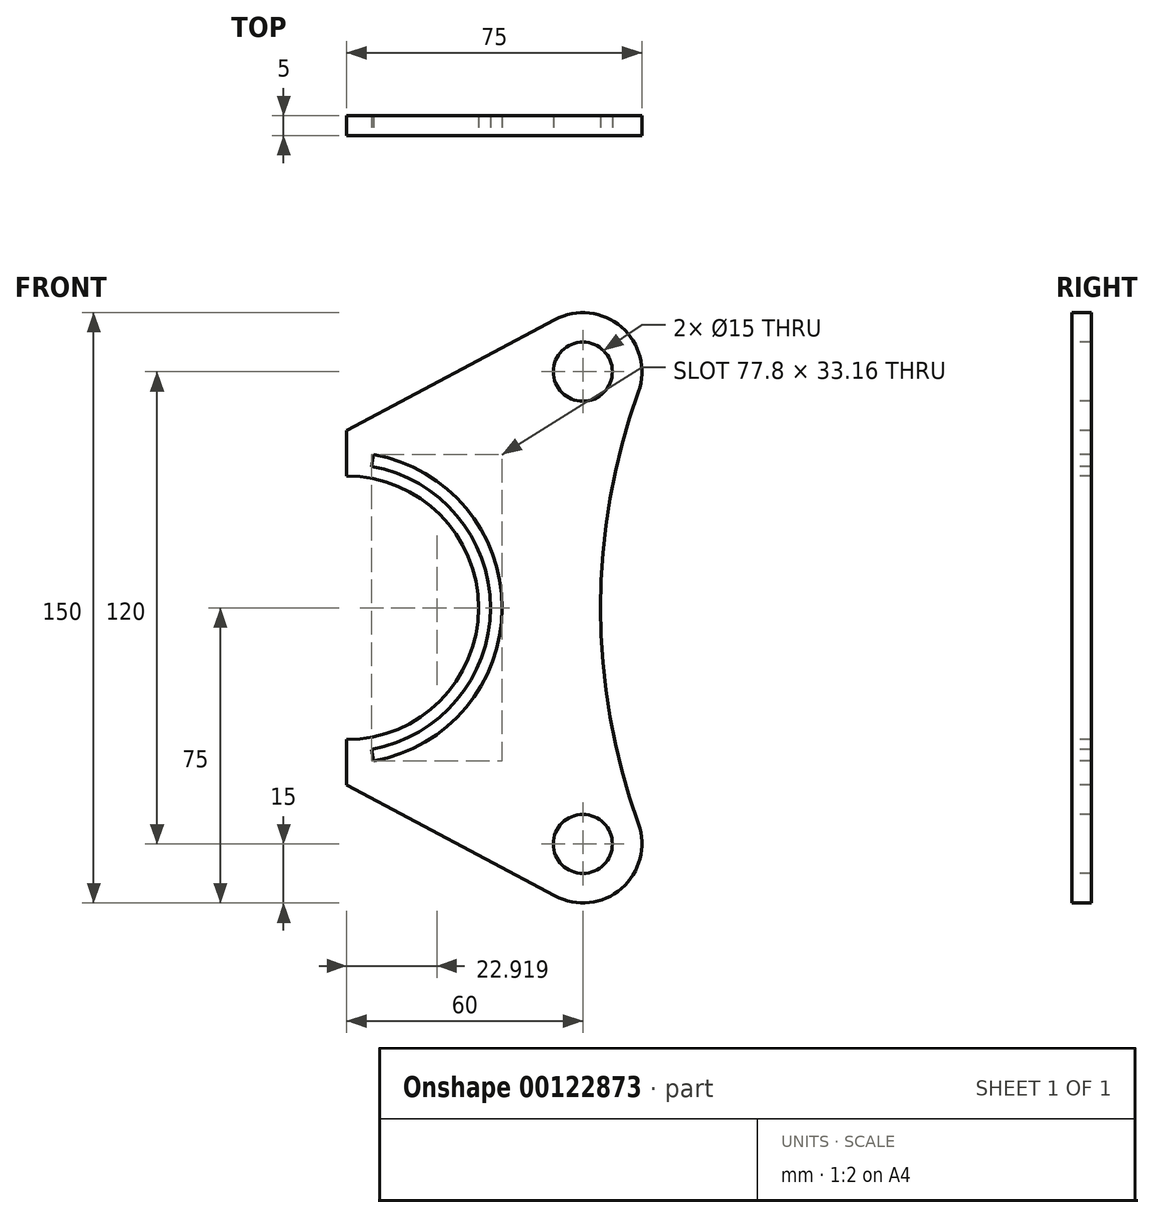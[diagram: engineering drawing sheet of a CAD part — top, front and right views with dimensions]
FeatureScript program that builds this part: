
annotation { "Feature Type Name" : "Feature", "Feature Type Description" : "" }
export const myFeature = defineFeature(function(context is Context, id is Id, definition is map)
    precondition{}
    {
        {
            var Q0;
            Q0=qCreatedBy(makeId("Front.planeOp"),FACE);
            var sketch = newSketch(context, id + "F0", { "sketchPlane" : qUnion([Q0])});
            skArc(sketch, "E0", {"start": v(-700, -33.5) * mm, "mid": v(-666.5, 0) * mm, "end": v(-700, 33.5) * mm});
            skCircle(sketch, "E1", {"center": v(0, 0) * mm, "radius": 642.8 * mm, "construction": true});
            skPoint(sketch, "E2", {"position": v(-640, 60) * mm});
            skPoint(sketch, "E3", {"position": v(-640, -60) * mm});
            skCircle(sketch, "E4", {"center": v(-640, 60) * mm, "radius": 7.5 * mm});
            skCircle(sketch, "E5", {"center": v(-640, -60) * mm, "radius": 7.5 * mm});
            skArc(sketch, "E6", {"start": v(-625.9, 54.9) * mm, "mid": v(-630.18, 71.34) * mm, "end": v(-647.06, 73.24) * mm});
            skArc(sketch, "E7", {"start": v(-647.06, -73.24) * mm, "mid": v(-630.18, -71.34) * mm, "end": v(-625.9, -54.9) * mm});
            skLineSegment(sketch, "E8", {"start": v(-700, 45) * mm, "end": v(-647.06, 73.24) * mm});
            skLineSegment(sketch, "E9", {"start": v(-647.06, -73.24) * mm, "end": v(-700, -45) * mm});
            skLineSegment(sketch, "E10", {"start": v(-700, -91.27) * mm, "end": v(-700, 112.6) * mm, "construction": true});
            skArc(sketch, "E11", {"start": v(-693.66, -35.95) * mm, "mid": v(-663.5, 0) * mm, "end": v(-693.66, 35.95) * mm});
            skArc(sketch, "E12", {"start": v(-693.14, -38.9) * mm, "mid": v(-660.5, 0) * mm, "end": v(-693.14, 38.9) * mm});
            skLineSegment(sketch, "E13", {"start": v(-700, 45) * mm, "end": v(-700, 33.5) * mm});
            skLineSegment(sketch, "E14", {"start": v(-700, -45) * mm, "end": v(-700, -33.5) * mm});
            skLineSegment(sketch, "E15", {"start": v(-700, 0) * mm, "end": v(-690.13, 55.95) * mm, "construction": true});
            skLineSegment(sketch, "E16", {"start": v(-700, 0) * mm, "end": v(-689.73, -58.24) * mm, "construction": true});
            skLineSegment(sketch, "E17", {"start": v(-693.66, -35.95) * mm, "end": v(-693.14, -38.9) * mm});
            skLineSegment(sketch, "E18", {"start": v(-693.14, 38.9) * mm, "end": v(-693.66, 35.95) * mm});
            skArc(sketch, "E19", {"start": v(-625.9, 54.9) * mm, "mid": v(-635.5, 0) * mm, "end": v(-625.9, -54.9) * mm});
            skSolve(sketch);
        }
        {
            var Q0;
            Q0=qSketchRegion(id+"F0",true);
            extrude(context, id + "F1", {"entities" : qUnion([Q0]), "oppositeDirection" : true, "depth" : 5 * mm});
        }
    });
